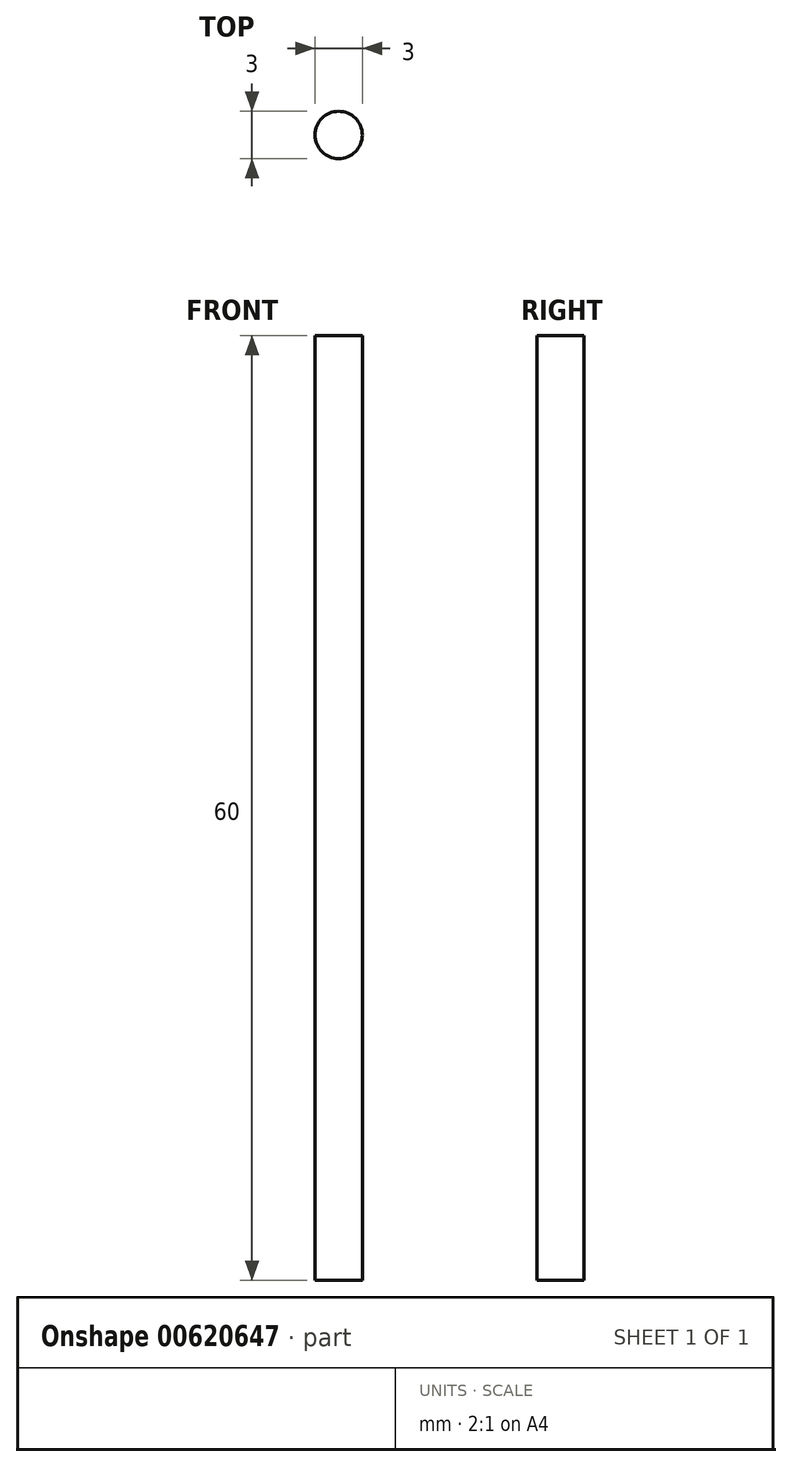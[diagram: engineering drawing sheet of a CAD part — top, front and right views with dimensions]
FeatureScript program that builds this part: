
annotation { "Feature Type Name" : "Feature", "Feature Type Description" : "" }
export const myFeature = defineFeature(function(context is Context, id is Id, definition is map)
    precondition{}
    {
        {
            var Q0;
            Q0=qCreatedBy(makeId("Top.planeOp"),FACE);
            var sketch = newSketch(context, id + "F0", { "sketchPlane" : qUnion([Q0])});
            skCircle(sketch, "E0", {"center": v(0, 0) * mm, "radius": 1.5 * mm});
            skSolve(sketch);
        }
        {
            var Q0;
            Q0=makeQuery(id+"F0.imprint","IMPRINT",FACE,{"disambiguationData":[TD([[makeQuery(id+"F0.imprint","IMPRINT",EDGE,{"derivedFrom":sQuery(id+"F0.wireOp",EDGE,"E0")}),1.0]])]});
            extrude(context, id + "F1", {"entities" : qUnion([Q0]), "depth" : 60 * mm, "offsetDistance" : 25 * mm});
        }
    });
